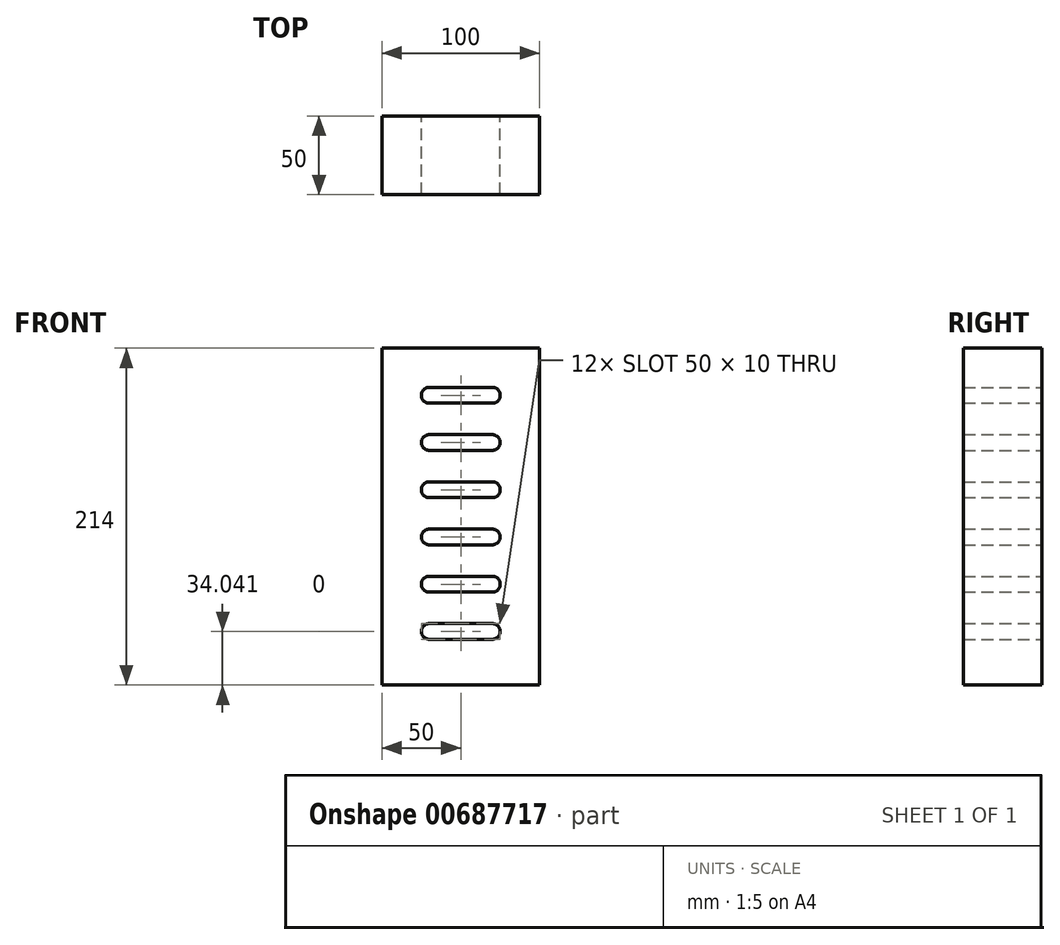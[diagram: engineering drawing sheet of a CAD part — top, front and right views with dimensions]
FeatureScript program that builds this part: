
annotation { "Feature Type Name" : "Feature", "Feature Type Description" : "" }
export const myFeature = defineFeature(function(context is Context, id is Id, definition is map)
    precondition{}
    {
        {
            var Q0;
            Q0=qCreatedBy(makeId("Front.planeOp"),FACE);
            var sketch = newSketch(context, id + "F0", { "sketchPlane" : qUnion([Q0])});
            skLineSegment(sketch, "E0", {"start": v(0, 0) * mm, "end": v(0, 214) * mm});
            skLineSegment(sketch, "E1", {"start": v(0, 214) * mm, "end": v(-100, 214) * mm});
            skLineSegment(sketch, "E2", {"start": v(-100, 0) * mm, "end": v(0, 0) * mm});
            skLineSegment(sketch, "E3", {"start": v(-100, 214) * mm, "end": v(-100, 184.04) * mm});
            skLineSegment(sketch, "E4", {"start": v(-100, 184.04) * mm, "end": v(-100, 154.04) * mm});
            skLineSegment(sketch, "E5", {"start": v(-100, 154.04) * mm, "end": v(-100, 124.04) * mm});
            skLineSegment(sketch, "E6", {"start": v(-100, 124.04) * mm, "end": v(-100, 94.04) * mm});
            skLineSegment(sketch, "E7", {"start": v(-100, 94.04) * mm, "end": v(-100, 64.04) * mm});
            skLineSegment(sketch, "E8", {"start": v(-100, 64.04) * mm, "end": v(-100, 34.04) * mm});
            skLineSegment(sketch, "E9", {"start": v(-100, 34.04) * mm, "end": v(-100, 0) * mm});
            skLineSegment(sketch, "E10", {"start": v(-100, 184.04) * mm, "end": v(-70, 184.04) * mm});
            skLineSegment(sketch, "E11", {"start": v(-70, 184.04) * mm, "end": v(-30, 184.04) * mm});
            skLineSegment(sketch, "E12", {"start": v(-30, 184.04) * mm, "end": v(0, 184.04) * mm});
            skLineSegment(sketch, "E13", {"start": v(-100, 154.04) * mm, "end": v(-70, 154.04) * mm});
            skLineSegment(sketch, "E14", {"start": v(-70, 154.04) * mm, "end": v(-30, 154.04) * mm});
            skLineSegment(sketch, "E15", {"start": v(-30, 154.04) * mm, "end": v(0, 154.04) * mm});
            skLineSegment(sketch, "E16", {"start": v(-100, 124.04) * mm, "end": v(-70, 124.04) * mm});
            skLineSegment(sketch, "E17", {"start": v(-70, 124.04) * mm, "end": v(-30, 124.04) * mm});
            skLineSegment(sketch, "E18", {"start": v(-30, 124.04) * mm, "end": v(0, 124.04) * mm});
            skLineSegment(sketch, "E19", {"start": v(-100, 94.04) * mm, "end": v(-70, 94.04) * mm});
            skLineSegment(sketch, "E20", {"start": v(-70, 94.04) * mm, "end": v(-30, 94.04) * mm});
            skLineSegment(sketch, "E21", {"start": v(-30, 94.04) * mm, "end": v(0, 94.04) * mm});
            skLineSegment(sketch, "E22", {"start": v(-100, 64.04) * mm, "end": v(-70, 64.04) * mm});
            skLineSegment(sketch, "E23", {"start": v(-70, 64.04) * mm, "end": v(-30, 64.04) * mm});
            skLineSegment(sketch, "E24", {"start": v(-30, 64.04) * mm, "end": v(0, 64.04) * mm});
            skLineSegment(sketch, "E25", {"start": v(-100, 34.04) * mm, "end": v(-70, 34.04) * mm});
            skLineSegment(sketch, "E26", {"start": v(-70, 34.04) * mm, "end": v(-30, 34.04) * mm});
            skLineSegment(sketch, "E27", {"start": v(-30, 34.04) * mm, "end": v(0, 34.04) * mm});
            skArc(sketch, "E28.0.startCap", {"start": v(-70, 149.04) * mm, "mid": v(-75, 154.04) * mm, "end": v(-70, 159.04) * mm});
            skArc(sketch, "E28.0.endCap", {"start": v(-30, 159.04) * mm, "mid": v(-25, 154.04) * mm, "end": v(-30, 149.04) * mm});
            skLineSegment(sketch, "E28.0.left", {"start": v(-70, 159.04) * mm, "end": v(-30, 159.04) * mm});
            skLineSegment(sketch, "E28.0.right", {"start": v(-70, 149.04) * mm, "end": v(-30, 149.04) * mm});
            skArc(sketch, "E28.1.startCap", {"start": v(-70, 119.04) * mm, "mid": v(-75, 124.04) * mm, "end": v(-70, 129.04) * mm});
            skArc(sketch, "E28.1.endCap", {"start": v(-30, 129.04) * mm, "mid": v(-25, 124.04) * mm, "end": v(-30, 119.04) * mm});
            skLineSegment(sketch, "E28.1.left", {"start": v(-70, 129.04) * mm, "end": v(-30, 129.04) * mm});
            skLineSegment(sketch, "E28.1.right", {"start": v(-70, 119.04) * mm, "end": v(-30, 119.04) * mm});
            skArc(sketch, "E28.2.startCap", {"start": v(-70, 89.04) * mm, "mid": v(-75, 94.04) * mm, "end": v(-70, 99.04) * mm});
            skArc(sketch, "E28.2.endCap", {"start": v(-30, 99.04) * mm, "mid": v(-25, 94.04) * mm, "end": v(-30, 89.04) * mm});
            skLineSegment(sketch, "E28.2.left", {"start": v(-70, 99.04) * mm, "end": v(-30, 99.04) * mm});
            skLineSegment(sketch, "E28.2.right", {"start": v(-70, 89.04) * mm, "end": v(-30, 89.04) * mm});
            skArc(sketch, "E28.3.startCap", {"start": v(-70, 59.04) * mm, "mid": v(-75, 64.04) * mm, "end": v(-70, 69.04) * mm});
            skArc(sketch, "E28.3.endCap", {"start": v(-30, 69.04) * mm, "mid": v(-25, 64.04) * mm, "end": v(-30, 59.04) * mm});
            skLineSegment(sketch, "E28.3.left", {"start": v(-70, 69.04) * mm, "end": v(-30, 69.04) * mm});
            skLineSegment(sketch, "E28.3.right", {"start": v(-70, 59.04) * mm, "end": v(-30, 59.04) * mm});
            skArc(sketch, "E28.4.startCap", {"start": v(-70, 29.04) * mm, "mid": v(-75, 34.04) * mm, "end": v(-70, 39.04) * mm});
            skArc(sketch, "E28.4.endCap", {"start": v(-30, 39.04) * mm, "mid": v(-25, 34.04) * mm, "end": v(-30, 29.04) * mm});
            skLineSegment(sketch, "E28.4.left", {"start": v(-70, 39.04) * mm, "end": v(-30, 39.04) * mm});
            skLineSegment(sketch, "E28.4.right", {"start": v(-70, 29.04) * mm, "end": v(-30, 29.04) * mm});
            skArc(sketch, "E29.0.startCap", {"start": v(-70, 179.04) * mm, "mid": v(-75, 184.04) * mm, "end": v(-70, 189.04) * mm});
            skArc(sketch, "E29.0.endCap", {"start": v(-30, 189.04) * mm, "mid": v(-25, 184.04) * mm, "end": v(-30, 179.04) * mm});
            skLineSegment(sketch, "E29.0.left", {"start": v(-70, 189.04) * mm, "end": v(-30, 189.04) * mm});
            skLineSegment(sketch, "E29.0.right", {"start": v(-70, 179.04) * mm, "end": v(-30, 179.04) * mm});
            skSolve(sketch);
        }
        {
            var Q0;
            {var subQ13=sQuery(id+"F0.wireOp",EDGE,"E5");Q0=makeQuery(id+"F0.imprint","IMPRINT",FACE,{"disambiguationData":[TD([[makeQuery(id+"F0.imprint","IMPRINT",EDGE,{"derivedFrom":subQ13}),1.0]])]});}
            var Q1;
            {var subQ13=sQuery(id+"F0.wireOp",EDGE,"E4");Q1=makeQuery(id+"F0.imprint","IMPRINT",FACE,{"disambiguationData":[TD([[makeQuery(id+"F0.imprint","IMPRINT",EDGE,{"derivedFrom":subQ13}),1.0]])]});}
            var Q2;
            {var subQ6=sQuery(id+"F0.wireOp",EDGE,"E1");Q2=makeQuery(id+"F0.imprint","IMPRINT",FACE,{"disambiguationData":[TD([[makeQuery(id+"F0.imprint","IMPRINT",EDGE,{"derivedFrom":subQ6}),1.0]])]});}
            var Q3;
            {var subQ9=sQuery(id+"F0.wireOp",EDGE,"E6");Q3=makeQuery(id+"F0.imprint","IMPRINT",FACE,{"disambiguationData":[TD([[makeQuery(id+"F0.imprint","IMPRINT",EDGE,{"derivedFrom":subQ9}),1.0]])]});}
            var Q4;
            {var subQ17=sQuery(id+"F0.wireOp",EDGE,"E7");Q4=makeQuery(id+"F0.imprint","IMPRINT",FACE,{"disambiguationData":[TD([[makeQuery(id+"F0.imprint","IMPRINT",EDGE,{"derivedFrom":subQ17}),1.0]])]});}
            var Q5;
            {var subQ8=sQuery(id+"F0.wireOp",EDGE,"E8");Q5=makeQuery(id+"F0.imprint","IMPRINT",FACE,{"disambiguationData":[TD([[makeQuery(id+"F0.imprint","IMPRINT",EDGE,{"derivedFrom":subQ8}),1.0]])]});}
            var Q6;
            {var subQ4=sQuery(id+"F0.wireOp",EDGE,"E2");Q6=makeQuery(id+"F0.imprint","IMPRINT",FACE,{"disambiguationData":[TD([[makeQuery(id+"F0.imprint","IMPRINT",EDGE,{"derivedFrom":subQ4}),1.0]])]});}
            extrude(context, id + "F1", {"entities" : qUnion([Q0, Q1, Q2, Q3, Q4, Q5, Q6]), "depth" : 50 * mm, "offsetDistance" : 25 * mm});
        }
    });
